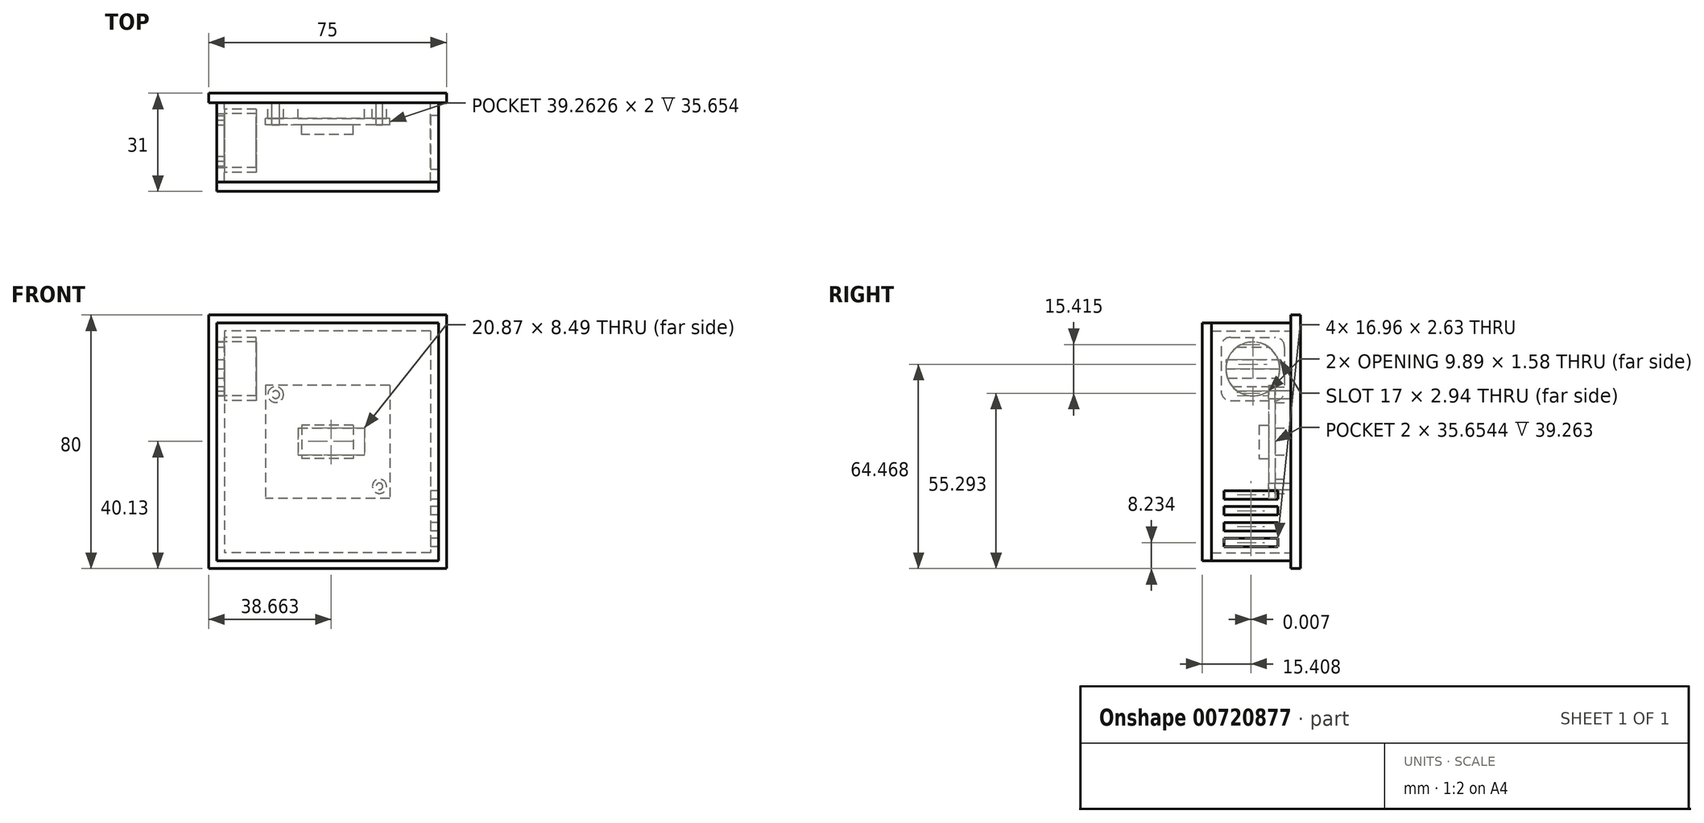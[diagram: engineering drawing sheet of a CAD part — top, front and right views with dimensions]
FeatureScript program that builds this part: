
annotation { "Feature Type Name" : "Feature", "Feature Type Description" : "" }
export const myFeature = defineFeature(function(context is Context, id is Id, definition is map)
    precondition{}
    {
        {
            var Q0;
            Q0=qCreatedBy(makeId("Front.planeOp"),FACE);
            var sketch = newSketch(context, id + "F0", { "sketchPlane" : qUnion([Q0])});
            skLineSegment(sketch, "E0.bottom", {"start": v(32.5, 35) * mm, "end": v(-32.5, 35) * mm});
            skLineSegment(sketch, "E0.top", {"start": v(32.5, -35) * mm, "end": v(-32.5, -35) * mm});
            skLineSegment(sketch, "E0.left", {"start": v(32.5, 35) * mm, "end": v(32.5, -35) * mm});
            skLineSegment(sketch, "E0.right", {"start": v(-32.5, 35) * mm, "end": v(-32.5, -35) * mm});
            skPoint(sketch, "E0.middle", {"position": v(0, 0) * mm});
            skLineSegment(sketch, "E1.bottom", {"start": v(35, 37.5) * mm, "end": v(-35, 37.5) * mm});
            skLineSegment(sketch, "E1.top", {"start": v(35, -37.5) * mm, "end": v(-35, -37.5) * mm});
            skLineSegment(sketch, "E1.left", {"start": v(35, 37.5) * mm, "end": v(35, -37.5) * mm});
            skLineSegment(sketch, "E1.right", {"start": v(-35, 37.5) * mm, "end": v(-35, -37.5) * mm});
            skLineSegment(sketch, "E2.bottom", {"start": v(37.5, 40) * mm, "end": v(-37.5, 40) * mm});
            skLineSegment(sketch, "E2.top", {"start": v(37.5, -40) * mm, "end": v(-37.5, -40) * mm});
            skLineSegment(sketch, "E2.left", {"start": v(37.5, 40) * mm, "end": v(37.5, -40) * mm});
            skLineSegment(sketch, "E2.right", {"start": v(-37.5, 40) * mm, "end": v(-37.5, -40) * mm});
            skSolve(sketch);
        }
        {
            var Q0;
            Q0=makeQuery(id+"F0.imprint","IMPRINT",FACE,{"disambiguationData":[TD([[makeQuery(id+"F0.imprint","IMPRINT",EDGE,{"derivedFrom":sQuery(id+"F0.wireOp",EDGE,"E0.bottom")}),-1.0]])]});
            extrude(context, id + "F1", {"entities" : qUnion([Q0]), "depth" : 25 * mm, "offsetDistance" : 25 * mm});
        }
        {
            var Q0;
            Q0=makeQuery(id+"F0.imprint","IMPRINT",FACE,{"disambiguationData":[TD([[makeQuery(id+"F0.imprint","IMPRINT",EDGE,{"derivedFrom":sQuery(id+"F0.wireOp",EDGE,"E1.bottom")}),-1.0]])]});
            var Q1;
            Q1=makeQuery(id+"F0.imprint","IMPRINT",FACE,{"disambiguationData":[TD([[makeQuery(id+"F0.imprint","IMPRINT",EDGE,{"derivedFrom":sQuery(id+"F0.wireOp",EDGE,"E0.bottom")}),1.0]])]});
            var Q2;
            Q2=makeQuery(id+"F0.imprint","IMPRINT",FACE,{"disambiguationData":[TD([[makeQuery(id+"F0.imprint","IMPRINT",EDGE,{"derivedFrom":sQuery(id+"F0.wireOp",EDGE,"E0.bottom")}),-1.0]])]});
            extrude(context, id + "F2", {"entities" : qUnion([Q0, Q1, Q2]), "operationType" : NewBodyOperationType.ADD, "oppositeDirection" : true, "depth" : 3 * mm, "offsetDistance" : 25 * mm});
        }
        {
            var Q0;
            Q0=makeQuery(id+"F0.imprint","IMPRINT",FACE,{"disambiguationData":[TD([[makeQuery(id+"F0.imprint","IMPRINT",EDGE,{"derivedFrom":sQuery(id+"F0.wireOp",EDGE,"E0.bottom")}),1.0]])]});
            var sketch = newSketch(context, id + "F3", { "sketchPlane" : qUnion([Q0])});
            skLineSegment(sketch, "E3.bottom", {"start": v(19.63, 17.83) * mm, "end": v(-19.63, 17.83) * mm});
            skLineSegment(sketch, "E3.top", {"start": v(19.63, -17.83) * mm, "end": v(-19.63, -17.83) * mm});
            skLineSegment(sketch, "E3.left", {"start": v(19.63, 17.83) * mm, "end": v(19.63, -17.83) * mm});
            skLineSegment(sketch, "E3.right", {"start": v(-19.63, 17.83) * mm, "end": v(-19.63, -17.83) * mm});
            skPoint(sketch, "E3.middle", {"position": v(0, 0) * mm});
            skCircle(sketch, "E4", {"center": v(-16.37, 14.9) * mm, "radius": 2.48 * mm});
            skCircle(sketch, "E5", {"center": v(16.37, -14.05) * mm, "radius": 2.25 * mm});
            skCircle(sketch, "E6", {"center": v(-16.37, 14.9) * mm, "radius": 1.23 * mm});
            skCircle(sketch, "E7", {"center": v(16.37, -14.05) * mm, "radius": 1.05 * mm});
            skLineSegment(sketch, "E8.bottom", {"start": v(-9.27, 4.38) * mm, "end": v(11.6, 4.38) * mm});
            skLineSegment(sketch, "E8.top", {"start": v(-9.27, -4.12) * mm, "end": v(11.6, -4.12) * mm});
            skLineSegment(sketch, "E8.left", {"start": v(-9.27, 4.38) * mm, "end": v(-9.27, -4.12) * mm});
            skLineSegment(sketch, "E8.right", {"start": v(11.6, 4.38) * mm, "end": v(11.6, -4.12) * mm});
            skSolve(sketch);
        }
        {
            var Q0;
            Q0=makeQuery(id+"F3.imprint","IMPRINT",FACE,{"disambiguationData":[TD([[makeQuery(id+"F3.imprint","IMPRINT",EDGE,{"derivedFrom":sQuery(id+"F3.wireOp",EDGE,"E4")}),1.0]])]});
            var Q1;
            Q1=makeQuery(id+"F3.imprint","IMPRINT",FACE,{"disambiguationData":[TD([[makeQuery(id+"F3.imprint","IMPRINT",EDGE,{"derivedFrom":sQuery(id+"F3.wireOp",EDGE,"E5")}),1.0]])]});
            var Q2;
            Q2=makeQuery(id+"F3.imprint","IMPRINT",FACE,{"disambiguationData":[TD([[makeQuery(id+"F3.imprint","IMPRINT",EDGE,{"derivedFrom":sQuery(id+"F3.wireOp",EDGE,"E8.bottom")}),-1.0]])]});
            extrude(context, id + "F4", {"entities" : qUnion([Q0, Q1, Q2]), "operationType" : NewBodyOperationType.ADD, "depth" : 5 * mm, "offsetDistance" : 25 * mm});
        }
        {
            var Q0;
            Q0=makeQuery(id+"F4.opExtrude","CAP_FACE",FACE,{"disambiguationData":[OSD([sQuery(id+"F3.wireOp",EDGE,"E4"),sQuery(id+"F3.wireOp",EDGE,"E6")])],"isStart":false});
            var sketch = newSketch(context, id + "F5", { "sketchPlane" : qUnion([Q0])});
            skLineSegment(sketch, "E9.0", {"start": v(19.63, 17.83) * mm, "end": v(-19.63, 17.83) * mm});
            skLineSegment(sketch, "E10.0", {"start": v(-19.63, 17.83) * mm, "end": v(-19.63, -17.83) * mm});
            skLineSegment(sketch, "E11.0", {"start": v(19.63, 17.83) * mm, "end": v(19.63, -17.83) * mm});
            skLineSegment(sketch, "E12.0", {"start": v(19.63, -17.83) * mm, "end": v(-19.63, -17.83) * mm});
            skCircle(sketch, "E13.0", {"center": v(-16.37, 14.9) * mm, "radius": 1.23 * mm});
            skCircle(sketch, "E14.0", {"center": v(16.37, -14.05) * mm, "radius": 1.05 * mm});
            skSolve(sketch);
        }
        {
            var Q0;
            Q0=makeQuery(id+"F5.imprint","IMPRINT",FACE,{"disambiguationData":[TD([[makeQuery(id+"F5.imprint","IMPRINT",EDGE,{"derivedFrom":sQuery(id+"F5.wireOp",EDGE,"E9.0")}),1.0]])]});
            var Q1;
            Q1=makeQuery(id+"F5.imprint","IMPRINT",FACE,{"disambiguationData":[TD([[makeQuery(id+"F5.imprint","IMPRINT",EDGE,{"derivedFrom":sQuery(id+"F5.wireOp",EDGE,"E13.0")}),-1.0]])]});
            extrude(context, id + "F6", {"entities" : qUnion([Q0, Q1]), "depth" : 2 * mm, "offsetDistance" : 25 * mm});
        }
        {
            var Q0;
            Q0=makeQuery(id+"F6.opExtrude","CAP_FACE",FACE,{"disambiguationData":[OSD([sQuery(id+"F5.wireOp",EDGE,"E9.0"),sQuery(id+"F5.wireOp",EDGE,"E10.0"),sQuery(id+"F5.wireOp",EDGE,"E11.0"),sQuery(id+"F5.wireOp",EDGE,"E12.0"),sQuery(id+"F5.wireOp",EDGE,"E13.0"),sQuery(id+"F5.wireOp",EDGE,"E14.0")])],"isStart":false});
            var sketch = newSketch(context, id + "F7", { "sketchPlane" : qUnion([Q0])});
            skLineSegment(sketch, "E15.bottom", {"start": v(8.13, 5.24) * mm, "end": v(-8.13, 5.24) * mm});
            skLineSegment(sketch, "E15.top", {"start": v(8.13, -5.24) * mm, "end": v(-8.13, -5.24) * mm});
            skLineSegment(sketch, "E15.left", {"start": v(8.13, 5.24) * mm, "end": v(8.13, -5.24) * mm});
            skLineSegment(sketch, "E15.right", {"start": v(-8.13, 5.24) * mm, "end": v(-8.13, -5.24) * mm});
            skPoint(sketch, "E15.middle", {"position": v(0, 0) * mm});
            skSolve(sketch);
        }
        {
            var Q0;
            Q0=makeQuery(id+"F7.imprint","IMPRINT",FACE,{"disambiguationData":[TD([[makeQuery(id+"F7.imprint","IMPRINT",EDGE,{"derivedFrom":sQuery(id+"F7.wireOp",EDGE,"E15.bottom")}),1.0]])]});
            extrude(context, id + "F8", {"entities" : qUnion([Q0]), "depth" : 3 * mm, "offsetDistance" : 25 * mm});
        }
        {
            var Q0;
            Q0=makeQuery(id+"F1.opExtrude","CAP_FACE",FACE,{"disambiguationData":[OSD([sQuery(id+"F0.wireOp",EDGE,"E0.bottom"),sQuery(id+"F0.wireOp",EDGE,"E0.top"),sQuery(id+"F0.wireOp",EDGE,"E0.left"),sQuery(id+"F0.wireOp",EDGE,"E0.right"),sQuery(id+"F0.wireOp",EDGE,"E1.bottom"),sQuery(id+"F0.wireOp",EDGE,"E1.top"),sQuery(id+"F0.wireOp",EDGE,"E1.left"),sQuery(id+"F0.wireOp",EDGE,"E1.right")])],"isStart":false});
            var sketch = newSketch(context, id + "F9", { "sketchPlane" : qUnion([Q0])});
            skLineSegment(sketch, "E16.bottom", {"start": v(-35, 37.5) * mm, "end": v(35, 37.5) * mm});
            skLineSegment(sketch, "E16.top", {"start": v(-35, -37.5) * mm, "end": v(35, -37.5) * mm});
            skLineSegment(sketch, "E16.left", {"start": v(-35, 37.5) * mm, "end": v(-35, -37.5) * mm});
            skLineSegment(sketch, "E16.right", {"start": v(35, 37.5) * mm, "end": v(35, -37.5) * mm});
            skSolve(sketch);
        }
        {
            var Q0;
            Q0=makeQuery(id+"F9.imprint","IMPRINT",FACE,{"disambiguationData":[TD([[makeQuery(id+"F9.imprint","IMPRINT",EDGE,{"derivedFrom":sQuery(id+"F9.wireOp",EDGE,"E16.bottom")}),-1.0]])]});
            var Q1;
            Q1=makeQuery(id+"F9.imprint","IMPRINT",FACE,{"disambiguationData":[TD([[makeQuery(id+"F9.imprint","IMPRINT",EDGE,{"derivedFrom":makeQuery(id+"F1.opExtrude","CAP_EDGE",EDGE,{"disambiguationData":[OSD([sQuery(id+"F0.wireOp",EDGE,"E0.bottom")])],"isStart":false})}),-1.0]])]});
            var Q2;
            Q2=makeQuery(id+"F9.imprint","IMPRINT",FACE,{"disambiguationData":[TD([[makeQuery(id+"F9.imprint","IMPRINT",EDGE,{"derivedFrom":makeQuery(id+"F1.opExtrude","CAP_EDGE",EDGE,{"disambiguationData":[OSD([sQuery(id+"F0.wireOp",EDGE,"E0.bottom")])],"isStart":false})}),1.0]])]});
            extrude(context, id + "F10", {"entities" : qUnion([Q0, Q1, Q2]), "depth" : 3 * mm, "offsetDistance" : 25 * mm});
        }
        {
            var Q0;
            Q0=makeQuery(id+"F8.opExtrude","CAP_FACE",FACE,{"disambiguationData":[OSD([sQuery(id+"F7.wireOp",EDGE,"E15.bottom"),sQuery(id+"F7.wireOp",EDGE,"E15.top"),sQuery(id+"F7.wireOp",EDGE,"E15.left"),sQuery(id+"F7.wireOp",EDGE,"E15.right")])],"isStart":false});
            var sketch = newSketch(context, id + "F11", { "sketchPlane" : qUnion([Q0])});
            skLineSegment(sketch, "E17.bottom", {"start": v(11, 7.5) * mm, "end": v(-11, 7.5) * mm});
            skLineSegment(sketch, "E17.top", {"start": v(11, -7.5) * mm, "end": v(-11, -7.5) * mm});
            skLineSegment(sketch, "E17.left", {"start": v(11, 7.5) * mm, "end": v(11, -7.5) * mm});
            skLineSegment(sketch, "E17.right", {"start": v(-11, 7.5) * mm, "end": v(-11, -7.5) * mm});
            skPoint(sketch, "E17.middle", {"position": v(0, 0) * mm});
            skSolve(sketch);
        }
        {
            var Q0;
            Q0=makeQuery(id+"F1.opExtrude","SWEPT_FACE",FACE,{"disambiguationData":[OSD([sQuery(id+"F0.wireOp",EDGE,"E0.right")])]});
            var sketch = newSketch(context, id + "F12", { "sketchPlane" : qUnion([Q0])});
            skLineSegment(sketch, "E18.bottom", {"start": v(-19, 33) * mm, "end": v(-5, 33) * mm});
            skLineSegment(sketch, "E18.top", {"start": v(-19, 13) * mm, "end": v(-5, 13) * mm});
            skLineSegment(sketch, "E18.left", {"start": v(-22, 30) * mm, "end": v(-22, 16) * mm});
            skLineSegment(sketch, "E18.right", {"start": v(-2, 30) * mm, "end": v(-2, 16) * mm});
            skPoint(sketch, "E19.visualSharp", {"position": v(-22, 33) * mm});
            skArc(sketch, "E19.filletArc", {"start": v(-19, 33) * mm, "mid": v(-21.12, 32.12) * mm, "end": v(-22, 30) * mm});
            skPoint(sketch, "E20.visualSharp", {"position": v(-2, 33) * mm});
            skArc(sketch, "E20.filletArc", {"start": v(-2, 30) * mm, "mid": v(-2.88, 32.12) * mm, "end": v(-5, 33) * mm});
            skPoint(sketch, "E21.visualSharp", {"position": v(-2, 13) * mm});
            skArc(sketch, "E21.filletArc", {"start": v(-5, 13) * mm, "mid": v(-2.88, 13.88) * mm, "end": v(-2, 16) * mm});
            skPoint(sketch, "E22.visualSharp", {"position": v(-22, 13) * mm});
            skArc(sketch, "E22.filletArc", {"start": v(-22, 16) * mm, "mid": v(-21.12, 13.88) * mm, "end": v(-19, 13) * mm});
            skCircle(sketch, "E23", {"center": v(-12, 23) * mm, "radius": 8.5 * mm});
            skPoint(sketch, "E23.centerSnap0", {"position": v(-12, 33) * mm});
            skPoint(sketch, "E23.centerSnap1", {"position": v(-22, 23) * mm});
            skLineSegment(sketch, "E24.bottom", {"start": v(-17.19, 31.7) * mm, "end": v(-7.06, 31.7) * mm});
            skLineSegment(sketch, "E24.top", {"start": v(-17.19, 29.92) * mm, "end": v(-7.06, 29.92) * mm});
            skLineSegment(sketch, "E24.left", {"start": v(-17.19, 31.7) * mm, "end": v(-17.19, 29.92) * mm});
            skLineSegment(sketch, "E24.right", {"start": v(-7.06, 31.7) * mm, "end": v(-7.06, 29.92) * mm});
            skLineSegment(sketch, "E25.bottom", {"start": v(-20.93, 28.51) * mm, "end": v(-2.9, 28.51) * mm});
            skLineSegment(sketch, "E25.top", {"start": v(-20.93, 25.94) * mm, "end": v(-2.9, 25.94) * mm});
            skLineSegment(sketch, "E25.left", {"start": v(-20.93, 28.51) * mm, "end": v(-20.93, 25.94) * mm});
            skLineSegment(sketch, "E25.right", {"start": v(-2.9, 28.51) * mm, "end": v(-2.9, 25.94) * mm});
            skLineSegment(sketch, "E26.bottom", {"start": v(-21, 23) * mm, "end": v(-2.9, 23) * mm});
            skLineSegment(sketch, "E26.top", {"start": v(-21, 24.18) * mm, "end": v(-2.9, 24.18) * mm});
            skLineSegment(sketch, "E26.left", {"start": v(-21, 23) * mm, "end": v(-21, 24.18) * mm});
            skLineSegment(sketch, "E26.right", {"start": v(-2.9, 23) * mm, "end": v(-2.9, 24.18) * mm});
            skLineSegment(sketch, "E27.MirrorCS", {"start": v(-17.19, 14.3) * mm, "end": v(-17.19, 16.08) * mm});
            skLineSegment(sketch, "E28.MirrorCS", {"start": v(-17.19, 14.3) * mm, "end": v(-7.06, 14.3) * mm});
            skLineSegment(sketch, "E29.MirrorCS", {"start": v(-17.19, 16.08) * mm, "end": v(-7.06, 16.08) * mm});
            skLineSegment(sketch, "E30.MirrorCS", {"start": v(-7.06, 14.3) * mm, "end": v(-7.06, 16.08) * mm});
            skLineSegment(sketch, "E31.MirrorCS", {"start": v(-2.9, 23) * mm, "end": v(-2.9, 21.82) * mm});
            skLineSegment(sketch, "E32.MirrorCS", {"start": v(-2.9, 17.49) * mm, "end": v(-2.9, 20.06) * mm});
            skLineSegment(sketch, "E33.MirrorCS", {"start": v(-20.93, 17.49) * mm, "end": v(-20.93, 20.06) * mm});
            skPoint(sketch, "E34.MirrorP", {"position": v(-12, 13) * mm});
            skLineSegment(sketch, "E35.MirrorCS", {"start": v(-21, 21.82) * mm, "end": v(-2.9, 21.82) * mm});
            skLineSegment(sketch, "E36.MirrorCS", {"start": v(-20.93, 20.06) * mm, "end": v(-2.9, 20.06) * mm});
            skLineSegment(sketch, "E37.MirrorCS", {"start": v(-20.93, 17.49) * mm, "end": v(-2.9, 17.49) * mm});
            skLineSegment(sketch, "E38.MirrorCS", {"start": v(-21, 23) * mm, "end": v(-21, 21.82) * mm});
            skSolve(sketch);
        }
        {
            var Q0;
            Q0=makeQuery(id+"F12.imprint","IMPRINT",FACE,{"disambiguationData":[TD([[makeQuery(id+"F12.imprint","IMPRINT",EDGE,{"derivedFrom":sQuery(id+"F12.wireOp",EDGE,"E18.bottom")}),-1.0]])]});
            var Q1;
            {var subQ5=sQuery(id+"F12.wireOp",EDGE,"E25.left");Q1=makeQuery(id+"F12.imprint","IMPRINT",FACE,{"disambiguationData":[TD([[makeQuery(id+"F12.imprint","IMPRINT",EDGE,{"derivedFrom":subQ5}),1.0]])]});}
            var Q2;
            Q2=makeQuery(id+"F12.imprint","IMPRINT",FACE,{"disambiguationData":[TD([[makeQuery(id+"F12.imprint","IMPRINT",EDGE,{"derivedFrom":sQuery(id+"F12.wireOp",EDGE,"E24.bottom")}),-1.0]])]});
            var Q3;
            {var subQ5=sQuery(id+"F12.wireOp",EDGE,"E25.right");Q3=makeQuery(id+"F12.imprint","IMPRINT",FACE,{"disambiguationData":[TD([[makeQuery(id+"F12.imprint","IMPRINT",EDGE,{"derivedFrom":subQ5}),-1.0]])]});}
            var Q4;
            {var subQ5=sQuery(id+"F12.wireOp",EDGE,"E26.right");Q4=makeQuery(id+"F12.imprint","IMPRINT",FACE,{"disambiguationData":[TD([[makeQuery(id+"F12.imprint","IMPRINT",EDGE,{"derivedFrom":subQ5}),1.0]])]});}
            var Q5;
            {var subQ5=sQuery(id+"F12.wireOp",EDGE,"E31.MirrorCS");Q5=makeQuery(id+"F12.imprint","IMPRINT",FACE,{"disambiguationData":[TD([[makeQuery(id+"F12.imprint","IMPRINT",EDGE,{"derivedFrom":subQ5}),-1.0]])]});}
            var Q6;
            {var subQ5=sQuery(id+"F12.wireOp",EDGE,"E32.MirrorCS");Q6=makeQuery(id+"F12.imprint","IMPRINT",FACE,{"disambiguationData":[TD([[makeQuery(id+"F12.imprint","IMPRINT",EDGE,{"derivedFrom":subQ5}),1.0]])]});}
            var Q7;
            {var subQ1=sQuery(id+"F12.wireOp",EDGE,"E27.MirrorCS");Q7=makeQuery(id+"F12.imprint","IMPRINT",FACE,{"disambiguationData":[TD([[makeQuery(id+"F12.imprint","IMPRINT",EDGE,{"derivedFrom":subQ1}),-1.0]])]});}
            var Q8;
            {var subQ5=sQuery(id+"F12.wireOp",EDGE,"E33.MirrorCS");Q8=makeQuery(id+"F12.imprint","IMPRINT",FACE,{"disambiguationData":[TD([[makeQuery(id+"F12.imprint","IMPRINT",EDGE,{"derivedFrom":subQ5}),-1.0]])]});}
            var Q9;
            {var subQ5=sQuery(id+"F12.wireOp",EDGE,"E38.MirrorCS");Q9=makeQuery(id+"F12.imprint","IMPRINT",FACE,{"disambiguationData":[TD([[makeQuery(id+"F12.imprint","IMPRINT",EDGE,{"derivedFrom":subQ5}),1.0]])]});}
            var Q10;
            {var subQ5=sQuery(id+"F12.wireOp",EDGE,"E26.left");Q10=makeQuery(id+"F12.imprint","IMPRINT",FACE,{"disambiguationData":[TD([[makeQuery(id+"F12.imprint","IMPRINT",EDGE,{"derivedFrom":subQ5}),-1.0]])]});}
            extrude(context, id + "F13", {"entities" : qUnion([Q0, Q1, Q2, Q3, Q4, Q5, Q6, Q7, Q8, Q9, Q10]), "depth" : 10 * mm, "offsetDistance" : 25 * mm});
        }
        {
            var Q0;
            {var subQ0=sQuery(id+"F12.wireOp",EDGE,"E29.MirrorCS");var subQ1=sQuery(id+"F12.wireOp",EDGE,"E23");var subQ3=makeQuery(id+"F12.imprint","INTERSECT",VERTEX,{"derivedFrom":[subQ1,subQ0]});Q0=makeQuery(id+"F12.imprint","IMPRINT",FACE,{"disambiguationData":[TD([[makeQuery(id+"F12.imprint","IMPRINT",EDGE,{"disambiguationData":[TD([[subQ3,-1.0]])],"derivedFrom":subQ1}),1.0]])]});}
            var Q1;
            {var subQ0=sQuery(id+"F12.wireOp",EDGE,"E36.MirrorCS");var subQ1=sQuery(id+"F12.wireOp",EDGE,"E23");var subQ2=makeQuery(id+"F12.imprint","INTERSECT",VERTEX,{"disambiguationData":[OD(0.0)],"derivedFrom":[subQ1,subQ0]});Q1=makeQuery(id+"F12.imprint","IMPRINT",FACE,{"disambiguationData":[TD([[makeQuery(id+"F12.imprint","IMPRINT",EDGE,{"disambiguationData":[TD([[subQ2,-1.0]])],"derivedFrom":subQ1}),1.0]])]});}
            var Q2;
            {var subQ0=sQuery(id+"F12.wireOp",EDGE,"E26.bottom");var subQ1=sQuery(id+"F12.wireOp",EDGE,"E23");var subQ2=makeQuery(id+"F12.imprint","INTERSECT",VERTEX,{"disambiguationData":[OD(1.0)],"derivedFrom":[subQ1,subQ0]});Q2=makeQuery(id+"F12.imprint","IMPRINT",FACE,{"disambiguationData":[TD([[makeQuery(id+"F12.imprint","IMPRINT",EDGE,{"disambiguationData":[TD([[subQ2,-1.0]])],"derivedFrom":subQ1}),1.0]])]});}
            var Q3;
            {var subQ0=sQuery(id+"F12.wireOp",EDGE,"E26.top");var subQ1=sQuery(id+"F12.wireOp",EDGE,"E23");var subQ2=makeQuery(id+"F12.imprint","INTERSECT",VERTEX,{"disambiguationData":[OD(0.0)],"derivedFrom":[subQ1,subQ0]});Q3=makeQuery(id+"F12.imprint","IMPRINT",FACE,{"disambiguationData":[TD([[makeQuery(id+"F12.imprint","IMPRINT",EDGE,{"disambiguationData":[TD([[subQ2,1.0]])],"derivedFrom":subQ1}),1.0]])]});}
            var Q4;
            {var subQ0=sQuery(id+"F12.wireOp",EDGE,"E25.top");var subQ1=sQuery(id+"F12.wireOp",EDGE,"E23");var subQ2=makeQuery(id+"F12.imprint","INTERSECT",VERTEX,{"disambiguationData":[OD(0.0)],"derivedFrom":[subQ1,subQ0]});Q4=makeQuery(id+"F12.imprint","IMPRINT",FACE,{"disambiguationData":[TD([[makeQuery(id+"F12.imprint","IMPRINT",EDGE,{"disambiguationData":[TD([[subQ2,-1.0]])],"derivedFrom":subQ1}),1.0]])]});}
            var Q5;
            {var subQ0=sQuery(id+"F12.wireOp",EDGE,"E24.top");var subQ1=sQuery(id+"F12.wireOp",EDGE,"E23");var subQ3=makeQuery(id+"F12.imprint","INTERSECT",VERTEX,{"derivedFrom":[subQ1,subQ0]});Q5=makeQuery(id+"F12.imprint","IMPRINT",FACE,{"disambiguationData":[TD([[makeQuery(id+"F12.imprint","IMPRINT",EDGE,{"disambiguationData":[TD([[subQ3,1.0]])],"derivedFrom":subQ1}),1.0]])]});}
            extrude(context, id + "F14", {"entities" : qUnion([Q0, Q1, Q2, Q3, Q4, Q5]), "operationType" : NewBodyOperationType.REMOVE, "endBound" : BoundingType.THROUGH_ALL, "oppositeDirection" : true, "depth" : 25 * mm, "offsetDistance" : 25 * mm});
        }
        {
            var Q0;
            Q0=makeQuery(id+"F1.opExtrude","SWEPT_FACE",FACE,{"disambiguationData":[OSD([sQuery(id+"F0.wireOp",EDGE,"E0.left")])]});
            var sketch = newSketch(context, id + "F15", { "sketchPlane" : qUnion([Q0])});
            skLineSegment(sketch, "E39.bottom", {"start": v(4.1, -15.45) * mm, "end": v(21.05, -15.45) * mm});
            skLineSegment(sketch, "E39.top", {"start": v(4.1, -18.08) * mm, "end": v(21.05, -18.08) * mm});
            skLineSegment(sketch, "E39.left", {"start": v(4.1, -15.45) * mm, "end": v(4.1, -18.08) * mm});
            skLineSegment(sketch, "E39.right", {"start": v(21.05, -15.45) * mm, "end": v(21.05, -18.08) * mm});
            skLineSegment(sketch, "E40.0.1.0", {"start": v(4.1, -20.45) * mm, "end": v(4.1, -23.08) * mm});
            skLineSegment(sketch, "E40.0.1.1", {"start": v(21.06, -20.45) * mm, "end": v(21.06, -23.08) * mm});
            skLineSegment(sketch, "E40.0.1.2", {"start": v(4.1, -23.08) * mm, "end": v(21.06, -23.08) * mm});
            skLineSegment(sketch, "E40.0.1.3", {"start": v(4.1, -20.45) * mm, "end": v(21.06, -20.45) * mm});
            skLineSegment(sketch, "E40.0.2.0", {"start": v(4.1, -25.45) * mm, "end": v(4.1, -28.08) * mm});
            skLineSegment(sketch, "E40.0.2.1", {"start": v(21.07, -25.45) * mm, "end": v(21.07, -28.08) * mm});
            skLineSegment(sketch, "E40.0.2.2", {"start": v(4.1, -28.08) * mm, "end": v(21.07, -28.08) * mm});
            skLineSegment(sketch, "E40.0.2.3", {"start": v(4.1, -25.45) * mm, "end": v(21.07, -25.45) * mm});
            skLineSegment(sketch, "E40.0.3.0", {"start": v(4.11, -30.45) * mm, "end": v(4.11, -33.08) * mm});
            skLineSegment(sketch, "E40.0.3.1", {"start": v(21.07, -30.45) * mm, "end": v(21.07, -33.08) * mm});
            skLineSegment(sketch, "E40.0.3.2", {"start": v(4.11, -33.08) * mm, "end": v(21.07, -33.08) * mm});
            skLineSegment(sketch, "E40.0.3.3", {"start": v(4.11, -30.45) * mm, "end": v(21.07, -30.45) * mm});
            skLineSegment(sketch, "E40.direction1", {"start": v(4.1, -18.08) * mm, "end": v(29.1, -18.08) * mm, "construction": true});
            skLineSegment(sketch, "E40.direction2", {"start": v(4.1, -18.08) * mm, "end": v(4.1, -23.08) * mm, "construction": true});
            skSolve(sketch);
        }
        {
            var Q0;
            Q0=makeQuery(id+"F15.imprint","IMPRINT",FACE,{"disambiguationData":[TD([[makeQuery(id+"F15.imprint","IMPRINT",EDGE,{"derivedFrom":sQuery(id+"F15.wireOp",EDGE,"E39.bottom")}),-1.0]])]});
            var Q1;
            Q1=makeQuery(id+"F15.imprint","IMPRINT",FACE,{"disambiguationData":[TD([[makeQuery(id+"F15.imprint","IMPRINT",EDGE,{"derivedFrom":sQuery(id+"F15.wireOp",EDGE,"E40.0.2.0")}),1.0]])]});
            var Q2;
            Q2=makeQuery(id+"F15.imprint","IMPRINT",FACE,{"disambiguationData":[TD([[makeQuery(id+"F15.imprint","IMPRINT",EDGE,{"derivedFrom":sQuery(id+"F15.wireOp",EDGE,"E40.0.3.0")}),1.0]])]});
            var Q3;
            Q3=makeQuery(id+"F15.imprint","IMPRINT",FACE,{"disambiguationData":[TD([[makeQuery(id+"F15.imprint","IMPRINT",EDGE,{"derivedFrom":sQuery(id+"F15.wireOp",EDGE,"E40.0.1.0")}),1.0]])]});
            extrude(context, id + "F16", {"entities" : qUnion([Q0, Q1, Q2, Q3]), "operationType" : NewBodyOperationType.REMOVE, "oppositeDirection" : true, "depth" : 25 * mm, "offsetDistance" : 25 * mm});
        }
        {
            var Q0;
            Q0=makeQuery(id+"F10.opExtrude","CAP_FACE",FACE,{"disambiguationData":[OSD([sQuery(id+"F9.wireOp",EDGE,"E16.bottom"),sQuery(id+"F9.wireOp",EDGE,"E16.top"),sQuery(id+"F9.wireOp",EDGE,"E16.left"),sQuery(id+"F9.wireOp",EDGE,"E16.right")])],"isStart":false});
            var sketch = newSketch(context, id + "F17", { "sketchPlane" : qUnion([Q0])});
            skLineSegment(sketch, "E41.0", {"start": v(-35, 37.5) * mm, "end": v(-35, -37.5) * mm});
            skLineSegment(sketch, "E42.0", {"start": v(35, 37.5) * mm, "end": v(-35, 37.5) * mm});
            skLineSegment(sketch, "E43.0", {"start": v(35, 37.5) * mm, "end": v(35, -37.5) * mm});
            skLineSegment(sketch, "E44.0", {"start": v(35, -37.5) * mm, "end": v(-35, -37.5) * mm});
            skSolve(sketch);
        }
        {
            var Q0;
            Q0=makeQuery(id+"F17.imprint","IMPRINT",FACE,{"disambiguationData":[TD([[makeQuery(id+"F17.imprint","IMPRINT",EDGE,{"derivedFrom":sQuery(id+"F17.wireOp",EDGE,"E41.0")}),1.0]])]});
            var Q1;
            Q1=makeQuery(id+"F2.opExtrude","CAP_FACE",FACE,{"disambiguationData":[OSD([sQuery(id+"F0.wireOp",EDGE,"E2.bottom"),sQuery(id+"F0.wireOp",EDGE,"E2.top"),sQuery(id+"F0.wireOp",EDGE,"E2.left"),sQuery(id+"F0.wireOp",EDGE,"E2.right")])],"isStart":false});
            extrude(context, id + "F18", {"entities" : qUnion([Q0]), "endBound" : BoundingType.UP_TO_SURFACE, "oppositeDirection" : true, "depth" : 25 * mm, "endBoundEntityFace" : qUnion([Q1]), "offsetDistance" : 25 * mm});
        }
        {
            var Q0;
            Q0=makeQuery(id+"F13.opExtrude","SWEPT_BODY",BODY,{"disambiguationData":[OSD([sQuery(id+"F12.wireOp",EDGE,"E18.bottom"),sQuery(id+"F12.wireOp",EDGE,"E18.top"),sQuery(id+"F12.wireOp",EDGE,"E18.left"),sQuery(id+"F12.wireOp",EDGE,"E18.right"),sQuery(id+"F12.wireOp",EDGE,"E19.filletArc"),sQuery(id+"F12.wireOp",EDGE,"E20.filletArc"),sQuery(id+"F12.wireOp",EDGE,"E21.filletArc"),sQuery(id+"F12.wireOp",EDGE,"E22.filletArc"),sQuery(id+"F12.wireOp",EDGE,"E23")])]});
            var Q1;
            Q1=makeQuery(id+"F10.opExtrude","SWEPT_BODY",BODY,{"disambiguationData":[OSD([sQuery(id+"F9.wireOp",EDGE,"E16.bottom"),sQuery(id+"F9.wireOp",EDGE,"E16.top"),sQuery(id+"F9.wireOp",EDGE,"E16.left"),sQuery(id+"F9.wireOp",EDGE,"E16.right")])]});
            var Q2;
            Q2=makeQuery(id+"F8.opExtrude","SWEPT_BODY",BODY,{"disambiguationData":[OSD([sQuery(id+"F7.wireOp",EDGE,"E15.bottom"),sQuery(id+"F7.wireOp",EDGE,"E15.top"),sQuery(id+"F7.wireOp",EDGE,"E15.left"),sQuery(id+"F7.wireOp",EDGE,"E15.right")])]});
            var Q3;
            Q3=makeQuery(id+"F6.opExtrude","SWEPT_BODY",BODY,{"disambiguationData":[OSD([sQuery(id+"F5.wireOp",EDGE,"E9.0"),sQuery(id+"F5.wireOp",EDGE,"E10.0"),sQuery(id+"F5.wireOp",EDGE,"E11.0"),sQuery(id+"F5.wireOp",EDGE,"E12.0"),sQuery(id+"F5.wireOp",EDGE,"E13.0"),sQuery(id+"F5.wireOp",EDGE,"E14.0")])]});
            var Q4;
            Q4=makeQuery(id+"F2.opExtrude","SWEPT_BODY",BODY,{"disambiguationData":[OSD([sQuery(id+"F0.wireOp",EDGE,"E2.bottom"),sQuery(id+"F0.wireOp",EDGE,"E2.top"),sQuery(id+"F0.wireOp",EDGE,"E2.left"),sQuery(id+"F0.wireOp",EDGE,"E2.right")])]});
            var Q5;
            Q5=makeQuery(id+"F1.opExtrude","SWEPT_BODY",BODY,{"disambiguationData":[OSD([sQuery(id+"F0.wireOp",EDGE,"E0.bottom"),sQuery(id+"F0.wireOp",EDGE,"E0.top"),sQuery(id+"F0.wireOp",EDGE,"E0.left"),sQuery(id+"F0.wireOp",EDGE,"E0.right"),sQuery(id+"F0.wireOp",EDGE,"E1.bottom"),sQuery(id+"F0.wireOp",EDGE,"E1.top"),sQuery(id+"F0.wireOp",EDGE,"E1.left"),sQuery(id+"F0.wireOp",EDGE,"E1.right")])]});
            var Q6;
            Q6=makeQuery(id+"F18.opExtrude","SWEPT_BODY",BODY,{"disambiguationData":[OSD([sQuery(id+"F17.wireOp",EDGE,"E41.0"),sQuery(id+"F17.wireOp",EDGE,"E42.0"),sQuery(id+"F17.wireOp",EDGE,"E43.0"),sQuery(id+"F17.wireOp",EDGE,"E44.0")])]});
            booleanBodies(context, id + "F19", {"operationType" : BooleanOperationType.SUBTRACTION, "tools" : qUnion([Q0, Q1, Q2, Q3, Q4, Q5]), "targets" : qUnion([Q6]), "keepTools" : true});
        }
    });
